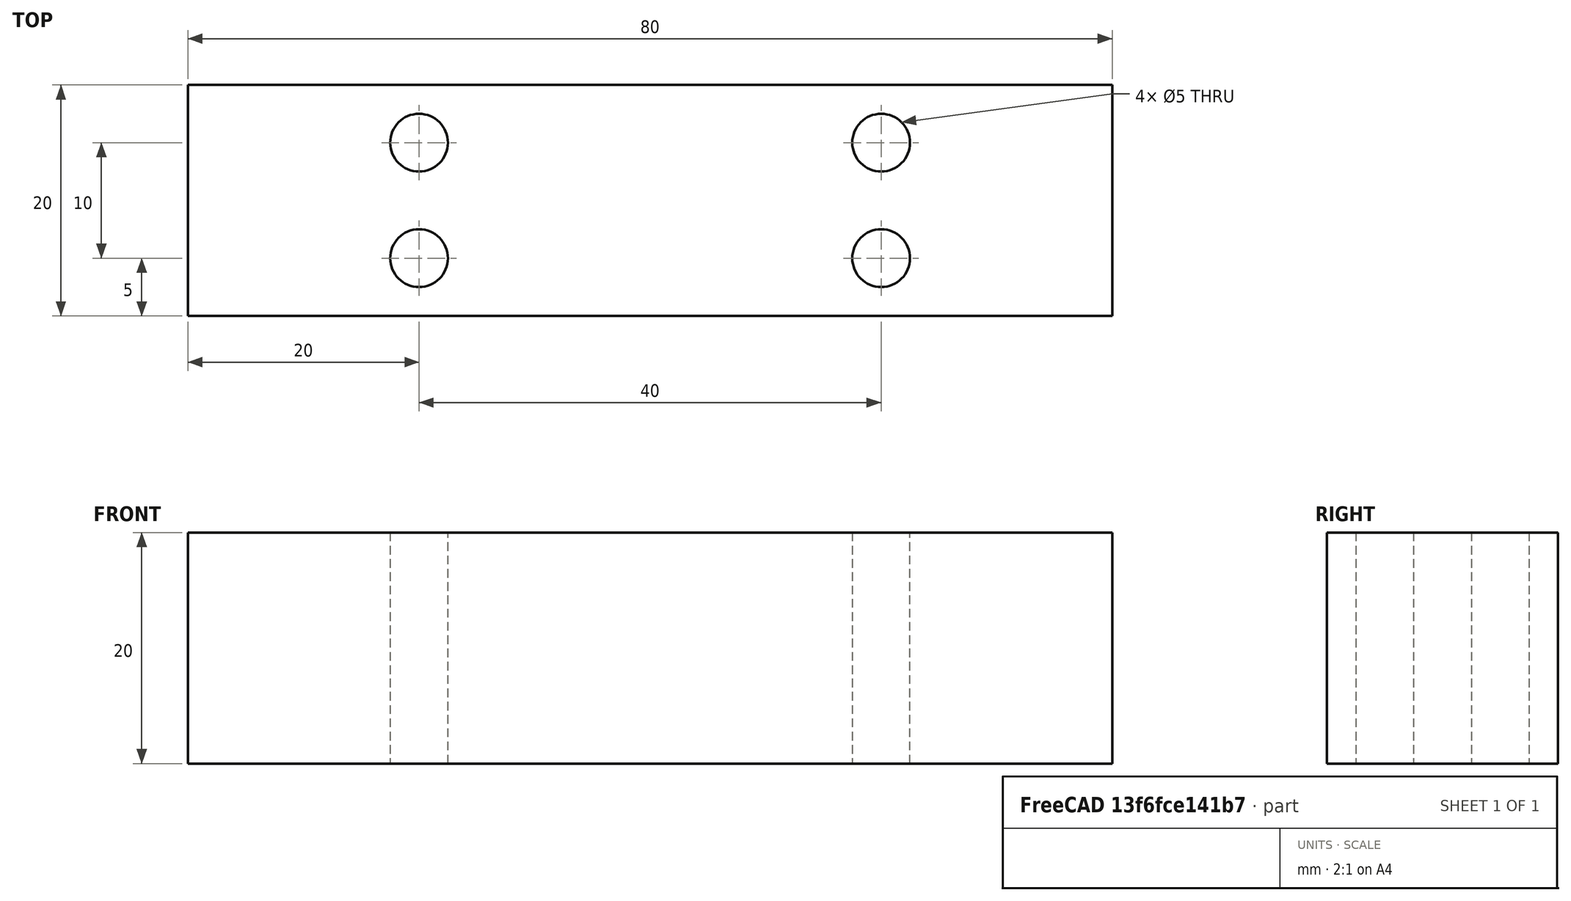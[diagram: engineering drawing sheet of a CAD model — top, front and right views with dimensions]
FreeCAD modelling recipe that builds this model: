
FCSTD DOCUMENT  (FreeCAD 0.18R16110 (Git))
Label: nutblock
License: All rights reserved
LicenseURL: http://en.wikipedia.org/wiki/All_rights_reserved
objects: Sketcher::SketchObject×1, PartDesign::Pad×1, PartDesign::Body×1
note: 4 computed .brp shape members not serialized (recipe doc carries the construction recipe); baked Part::Feature solids carry a one-line shape summary decoded from their .brp

FEATURE [Sketcher::SketchObject] Sketch
  MapMode = 5
  Support = -> [XY_Plane]
  sketch-geometry (8):
    g0: LineSegment StartX=0 StartY=20 StartZ=0 EndX=80 EndY=20 EndZ=0
    g1: LineSegment StartX=80 StartY=20 StartZ=0 EndX=80 EndY=0 EndZ=0
    g2: LineSegment StartX=80 StartY=0 StartZ=0 EndX=0 EndY=0 EndZ=0
    g3: LineSegment StartX=0 StartY=0 StartZ=0 EndX=0 EndY=20 EndZ=0
    g4: Circle CenterX=20 CenterY=15 CenterZ=0 NormalX=0 NormalY=0 NormalZ=1 AngleXU=0 Radius=2.5
    g5: Circle CenterX=20 CenterY=5 CenterZ=0 NormalX=0 NormalY=0 NormalZ=1 AngleXU=0 Radius=2.5
    g6: Circle CenterX=60 CenterY=15 CenterZ=0 NormalX=0 NormalY=0 NormalZ=1 AngleXU=0 Radius=2.5
    g7: Circle CenterX=60 CenterY=5 CenterZ=0 NormalX=0 NormalY=0 NormalZ=1 AngleXU=0 Radius=2.5
  constraints (23):
    c: Coincident(g0,g1)
    c: Coincident(g1,g2)
    c: Coincident(g2,g3)
    c: Coincident(g3,g0)
    c: Horizontal(g0)
    c: Horizontal(g2)
    c: Vertical(g1)
    c: Vertical(g3)
    c: DistanceX(g0,g0) = 80
    c: DistanceY(g3,g3) = 20
    c: Coincident(g2,g-1)
    c: DistanceX(g2,g5) = 20
    c: DistanceX(g4,g5) = 0
    c: DistanceX(g4,g6) = 40
    c: DistanceX(g6,g7) = 0
    c: DistanceY(g2,g5) = 5
    c: DistanceY(g5,g4) = 10
    c: DistanceY(g5,g7) = 0
    c: DistanceY(g4,g6) = 0
    c: Radius(g4) = 2.5  'kernloch_m6'
    c: Equal(g4,g6)
    c: Equal(g4,g7)
    c: Equal(g4,g5)
FEATURE [PartDesign::Pad] Pad
  Length = 20
  Length2 = 100
  Profile = -> Sketch
  Type = 0
FEATURE [PartDesign::Body] Body
  Group = -> [Sketch,Pad]
  Origin = -> Origin
  Tip = -> Pad
